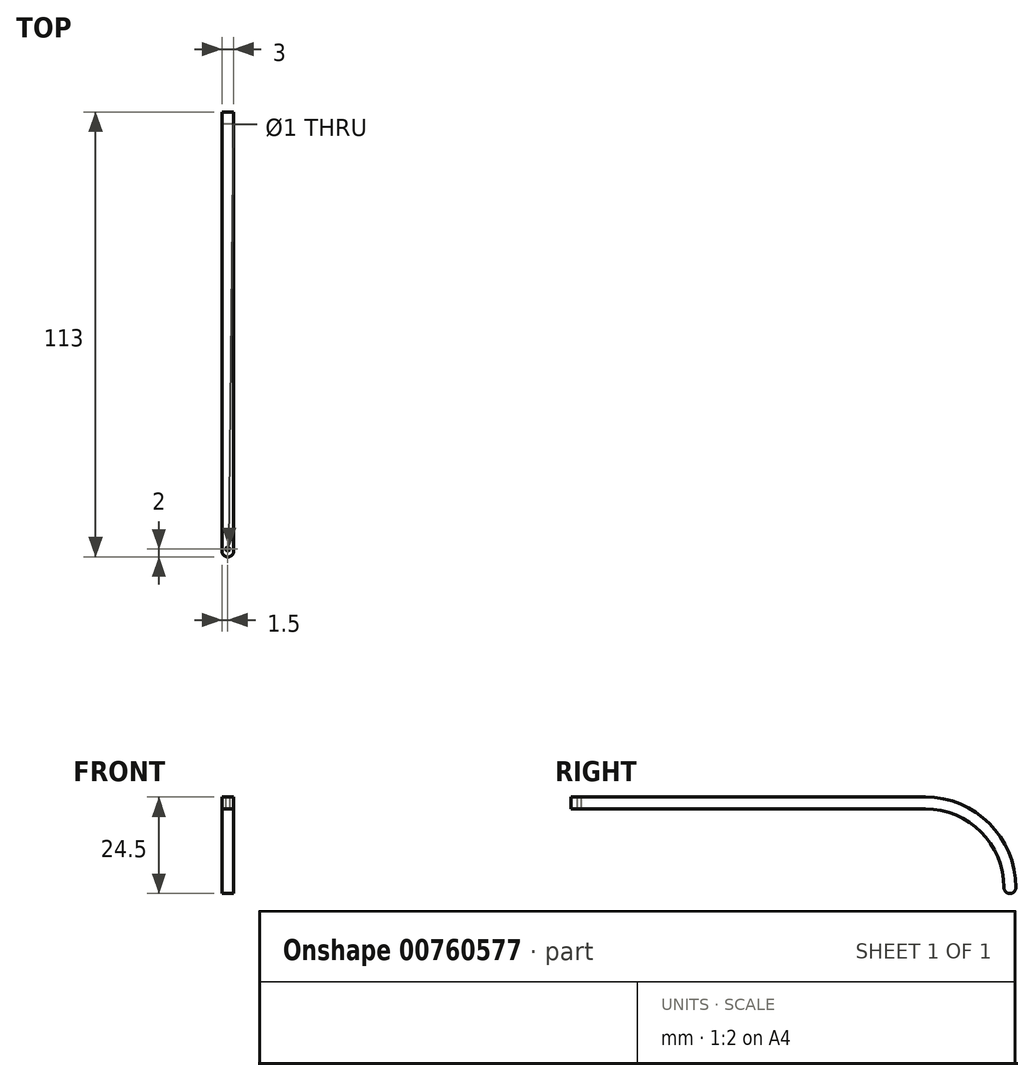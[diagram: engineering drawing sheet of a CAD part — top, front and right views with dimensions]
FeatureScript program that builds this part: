
annotation { "Feature Type Name" : "Feature", "Feature Type Description" : "" }
export const myFeature = defineFeature(function(context is Context, id is Id, definition is map)
    precondition{}
    {
        {
            var Q0;
            Q0=qCreatedBy(makeId("Right.planeOp"),FACE);
            var sketch = newSketch(context, id + "F0", { "sketchPlane" : qUnion([Q0])});
            skLineSegment(sketch, "E0.bottom", {"start": v(-45, 0) * mm, "end": v(45, 0) * mm});
            skLineSegment(sketch, "E0.top", {"start": v(-45, 3) * mm, "end": v(45, 3) * mm});
            skLineSegment(sketch, "E0.left", {"start": v(-45, 0) * mm, "end": v(-45, 3) * mm});
            skArc(sketch, "E1", {"start": v(45, 0) * mm, "mid": v(59.14, -5.86) * mm, "end": v(65, -20) * mm});
            skArc(sketch, "E2", {"start": v(45, 3) * mm, "mid": v(61.26, -3.74) * mm, "end": v(68, -20) * mm});
            skArc(sketch, "E3", {"start": v(68, -20) * mm, "mid": v(66.5, -21.5) * mm, "end": v(65, -20) * mm});
            skSolve(sketch);
        }
        {
            var Q0;
            Q0 = qSketchRegion(id + "F0", true);
            extrude(context, id + "F1", {"entities" : qUnion([Q0]), "depth" : 3 * mm, "offsetDistance" : 25 * mm});
        }
        {
            var Q0;
            Q0=qCreatedBy(makeId("Top.planeOp"),FACE);
            var sketch = newSketch(context, id + "F2", { "sketchPlane" : qUnion([Q0])});
            skCircle(sketch, "E4", {"center": v(1.5, -43) * mm, "radius": 0.5 * mm});
            skSolve(sketch);
        }
        {
            var Q0;
            Q0=sQuery(id+"F2.wireOp",VERTEX,"E4.center");
            var Q1;
            Q1=makeQuery(id+"F1.opExtrude","SWEPT_BODY",BODY,{"disambiguationData":[OSD([sQuery(id+"F0.wireOp",EDGE,"E0.bottom"),sQuery(id+"F0.wireOp",EDGE,"E0.top"),sQuery(id+"F0.wireOp",EDGE,"E0.left"),sQuery(id+"F0.wireOp",EDGE,"E1"),sQuery(id+"F0.wireOp",EDGE,"E2"),sQuery(id+"F0.wireOp",EDGE,"E3")])]});
            hole(context, id + "F3", {"style" : HoleStyle.SIMPLE, "endStyle" : HoleEndStyle.THROUGH, "oppositeDirection" : true, "holeDiameter" : 1 * mm, "majorDiameter" : 5 * mm, "isTappedThrough" : true, "tappedDepth" : 12 * mm, "tapClearance" : 3, "locations" : qUnion([Q0]), "scope" : qUnion([Q1])});
        }
        {
            var Q0;
            Q0=makeQuery(id+"F1.opExtrude","CAP_EDGE",EDGE,{"disambiguationData":[OSD([sQuery(id+"F0.wireOp",EDGE,"E0.left")])],"isStart":false});
            var Q1;
            Q1=makeQuery(id+"F1.opExtrude","CAP_EDGE",EDGE,{"disambiguationData":[OSD([sQuery(id+"F0.wireOp",EDGE,"E0.left")])],"isStart":true});
            fillet(context, id + "F4", {"entities" : qUnion([Q0, Q1]), "radius" : 1.5 * mm, "tangentPropagation" : true, "allowEdgeOverflow" : false});
        }
    });
